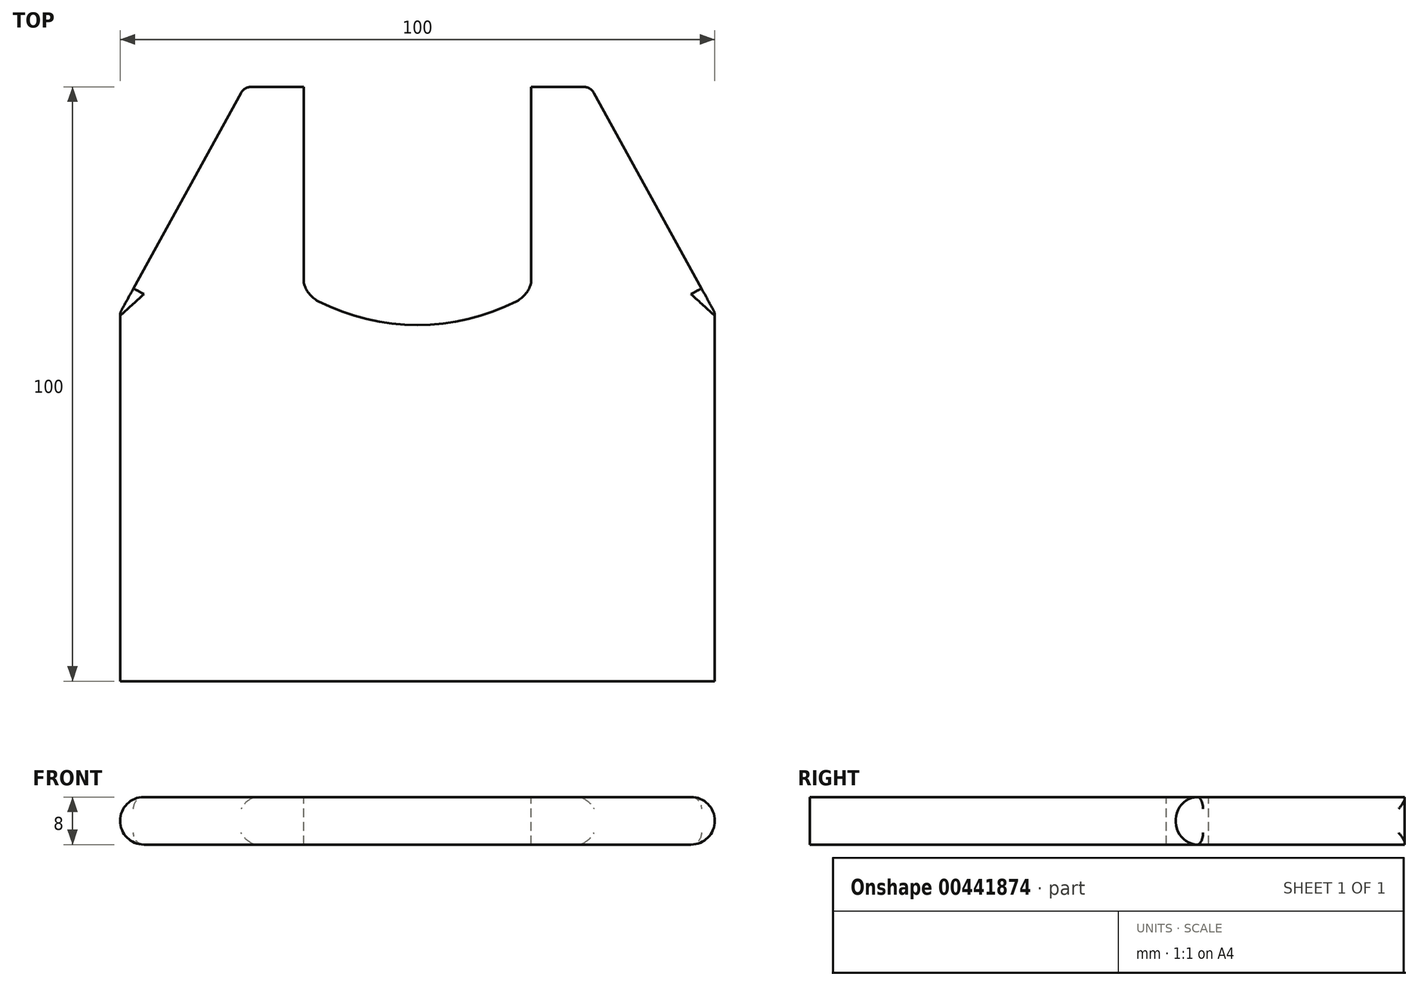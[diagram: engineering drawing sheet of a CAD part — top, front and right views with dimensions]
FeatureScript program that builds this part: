
annotation { "Feature Type Name" : "Feature", "Feature Type Description" : "" }
export const myFeature = defineFeature(function(context is Context, id is Id, definition is map)
    precondition{}
    {
        {
            var Q0;
            Q0=qCreatedBy(makeId("Front.planeOp"),FACE);
            var sketch = newSketch(context, id + "F0", { "sketchPlane" : qUnion([Q0])});
            skLineSegment(sketch, "E0.bottom", {"start": v(46, -4) * mm, "end": v(-46, -4) * mm});
            skLineSegment(sketch, "E0.top", {"start": v(46, 4) * mm, "end": v(-46, 4) * mm});
            skPoint(sketch, "E0.middle", {"position": v(0, 0) * mm});
            skArc(sketch, "E1", {"start": v(46, -4) * mm, "mid": v(50, 0) * mm, "end": v(46, 4) * mm});
            skArc(sketch, "E2", {"start": v(-46, 4) * mm, "mid": v(-50, 0) * mm, "end": v(-46, -4) * mm});
            skSolve(sketch);
        }
        {
            var Q0;
            Q0 = qSketchRegion(id + "F0", true);
            extrude(context, id + "F1", {"entities" : qUnion([Q0]), "depth" : 100 * mm, "offsetDistance" : 25 * mm});
        }
        {
            var Q0;
            Q0=makeQuery(id+"F1.opExtrude","SWEPT_FACE",FACE,{"disambiguationData":[OSD([sQuery(id+"F0.wireOp",EDGE,"E0.top")])]});
            var sketch = newSketch(context, id + "F2", { "sketchPlane" : qUnion([Q0])});
            skLineSegment(sketch, "E3.top", {"start": v(19.1, 48.04) * mm, "end": v(-19.1, 48.04) * mm});
            skLineSegment(sketch, "E3.left", {"start": v(19.1, -32.95) * mm, "end": v(19.1, 48.04) * mm});
            skLineSegment(sketch, "E3.right", {"start": v(-19.1, -32.95) * mm, "end": v(-19.1, 48.04) * mm});
            skPoint(sketch, "E3.middle", {"position": v(0, 0) * mm});
            skArc(sketch, "E4", {"start": v(-16.7, -36.06) * mm, "mid": v(0, -40.08) * mm, "end": v(16.7, -36.06) * mm});
            skArc(sketch, "E5", {"start": v(-19.1, -32.95) * mm, "mid": v(-18.25, -34.77) * mm, "end": v(-16.7, -36.06) * mm});
            skLineSegment(sketch, "E6", {"start": v(0, -22.7) * mm, "end": v(0, -47.16) * mm, "construction": true});
            skArc(sketch, "E7.MirrorCS", {"start": v(19.1, -32.95) * mm, "mid": v(18.25, -34.77) * mm, "end": v(16.7, -36.06) * mm});
            skSolve(sketch);
        }
        {
            var Q0;
            Q0 = qSketchRegion(id + "F2", true);
            extrude(context, id + "F3", {"entities" : qUnion([Q0]), "operationType" : NewBodyOperationType.REMOVE, "oppositeDirection" : true, "depth" : 25 * mm, "offsetDistance" : 25 * mm});
        }
        {
            var Q0;
            Q0=makeQuery(id+"F1.opExtrude","SWEPT_FACE",FACE,{"disambiguationData":[OSD([sQuery(id+"F0.wireOp",EDGE,"E0.bottom")])]});
            var sketch = newSketch(context, id + "F4", { "sketchPlane" : qUnion([Q0])});
            skLineSegment(sketch, "E8", {"start": v(29.1, 0) * mm, "end": v(50, 38) * mm});
            skLineSegment(sketch, "E9", {"start": v(50, 140) * mm, "end": v(50, 0) * mm, "construction": true});
            skLineSegment(sketch, "E10", {"start": v(0, 100) * mm, "end": v(0, -25.17) * mm, "construction": true});
            skLineSegment(sketch, "E11.MirrorCS", {"start": v(-29.1, 0) * mm, "end": v(-50, 38) * mm});
            skArc(sketch, "E12", {"start": v(29.1, 0) * mm, "mid": v(83.7, -5.28) * mm, "end": v(50, 38) * mm});
            skArc(sketch, "E13.MirrorCS", {"start": v(-29.1, 0) * mm, "mid": v(-83.7, -5.28) * mm, "end": v(-50, 38) * mm});
            skSolve(sketch);
        }
        {
            var Q0;
            Q0 = qSketchRegion(id + "F4", true);
            extrude(context, id + "F5", {"entities" : qUnion([Q0]), "operationType" : NewBodyOperationType.REMOVE, "oppositeDirection" : true, "depth" : 25 * mm, "offsetDistance" : 25 * mm});
        }
        {
            var Q0;
            Q0=makeQuery(id+"F5.boolean.opBoolean","COPY",FACE,{"derivedFrom":makeQuery(id+"F5.opExtrude","SWEPT_FACE",FACE,{"disambiguationData":[OSD([sQuery(id+"F4.wireOp",EDGE,"E11.MirrorCS")])]})});
            var Q1;
            Q1=makeQuery(id+"F5.boolean.opBoolean","COPY",FACE,{"derivedFrom":makeQuery(id+"F5.opExtrude","SWEPT_FACE",FACE,{"disambiguationData":[OSD([sQuery(id+"F4.wireOp",EDGE,"E8")])]})});
            fillet(context, id + "F6", {"entities" : qUnion([Q0, Q1]), "radius" : 2 * mm, "tangentPropagation" : true, "allowEdgeOverflow" : false});
        }
    });
